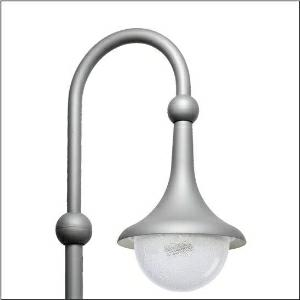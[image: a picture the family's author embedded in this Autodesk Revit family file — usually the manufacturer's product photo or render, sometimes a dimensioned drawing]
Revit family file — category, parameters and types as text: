
# Revit family: grosse_glocke___st1_2a_5xa1563e1b208_1d7c
name_source: partatom
category: Lighting Fixtures
units: mm (PartAtom-declared; Revit-internal decimal feet)

## family parameters
Cut with Voids When Loaded = No
Host = Face
Light Source = No
Part Type = Normal
Room Calculation Point = No
Round Connector Dimension = Use Diameter
Shared = No

## types (1)
- --- (1 x LED, 3210 lm, 23.4 W, 3000K)
    Apparent Load = 23 VA
    CIE Flux Codes = 29 66 94 99 100
    Color Rendering = 70
    Color Temperature = 3000K
    Default Elevation = 1800 mm
    Description = Large Bell, mast luminaire, primary light control with 3 zone facetted reflector, of plastic, silver coated, primary optical cover: enclosure, of PMMA, transparent structured, light distribution: ST1.2a, light emission: direct distribution, primary light characteristic: asymmetric, installation type: suspended mounting, LED High Power LED, rated luminous flux: 3.210 lm, light colour: 730, colour temperature: 3000K, control gear: ECG Plus, control: flexible luminous flux parameterisation, time-dependent luminous flux control, constant luminous flux control, digital communication interface, power reduction, electronic power reduction, mains connection: 220..240V, AC, 50/60Hz, start of lifetime: 23 W, end of lifetime: 24 W, reduction: 12 W, luminaire housing, bell-shaped, of glass-fibre reinforced polyester, coated, Siteco® metallic grey (DB 702S), diameter: 530 mm, height: 695mm, protection rating (complete): IP54, insulation class (complete): insulation class II (safety insulation), certification: CE, ENEC, VDE, impact resistance: IK08, standard-compliant lighting for roads and squares, packaging unit: 1 piece

Light Distribution: ST1.2a
    Height = 695 mm
    Lamp = 1 x LED
    Lamp Light Flux = 3210 lm
    Lamp Power = 23.4 W
    Lamp count = 1
    Length = 530 mm
    Luminous efficacy = 137 lm/W
    Manufacturer = Siteco
    ModVariant = No
    Model = 5XA1563E1B208
    Number of Poles = 1
    OnlyDefault = Yes
    Power Factor = 1
    Product Name = Große Glocke | ST1.2a
    Product group = mast luminaire | pylon annexe
    ProductGroupID = 6200
    Protection Class = Protection class II
    Protection Degree = IP 54
    RLX_Detail_Level = 1
    RlxData = <blob elided: 54861 chars, md5=0d7cbab7>
    Socket = socket
    Standby Power = 0 W
    System Light Flux = 3210 lm
    System Power = 23 W
    Type Comments = factory setting: luminous flux: 100 % | dim-lin: 254 | 460 mA
    Type Image = l_1005951.jpg
    URL = http://relux.com
    VarID = @adj_070171
    Voltage = 0 V
    Weight = 0.00 kg
    Width = 0 mm  [stored 0 ft]

note: [stored X ft] marks values corroborated as IEEE doubles in the binary element streams (Revit-internal decimal feet)

## geometry (parser evidence)
native form markers: Blend x4, Sweep x9
no freeform markers — native parametric forms only
